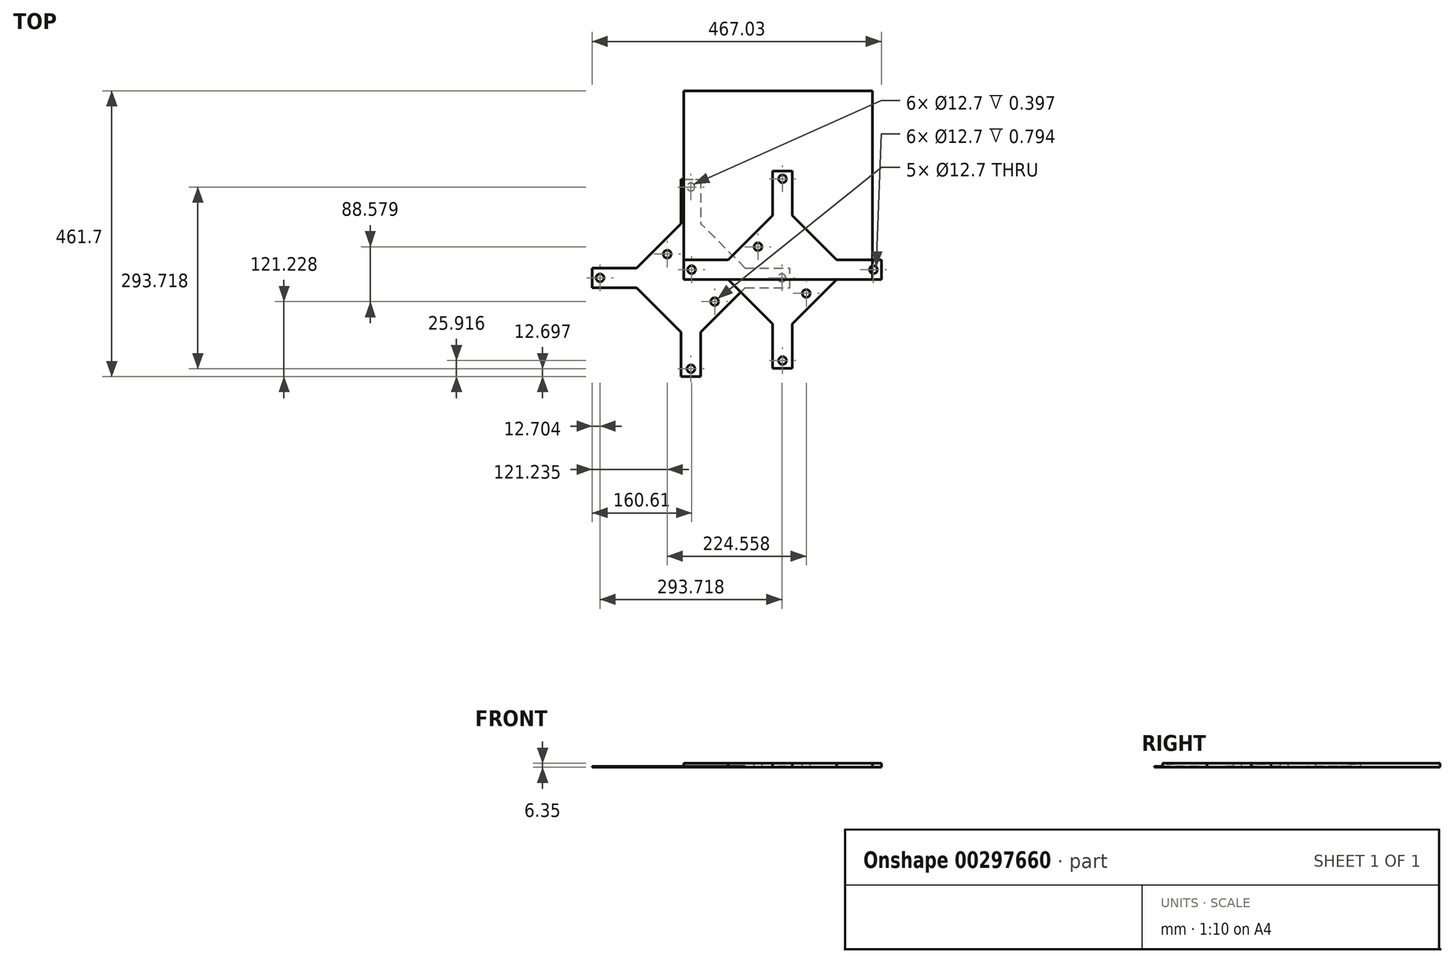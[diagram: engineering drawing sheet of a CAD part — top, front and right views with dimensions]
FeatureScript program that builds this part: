
annotation { "Feature Type Name" : "Feature", "Feature Type Description" : "" }
export const myFeature = defineFeature(function(context is Context, id is Id, definition is map)
    precondition{}
    {
        {
            var Q0;
            Q0=qCreatedBy(makeId("Top.planeOp"),FACE);
            var sketch = newSketch(context, id + "F0", { "sketchPlane" : qUnion([Q0])});
            skLineSegment(sketch, "E0.bottom", {"start": v(0, 0) * mm, "end": v(304.8, 0) * mm});
            skLineSegment(sketch, "E0.top", {"start": v(0, 304.8) * mm, "end": v(304.8, 304.8) * mm});
            skLineSegment(sketch, "E0.left", {"start": v(0, 0) * mm, "end": v(0, 304.8) * mm});
            skLineSegment(sketch, "E0.right", {"start": v(304.8, 0) * mm, "end": v(304.8, 304.8) * mm});
            skSolve(sketch);
        }
        {
            var Q0;
            Q0 = qSketchRegion(id + "F0", true);
            extrude(context, id + "F1", {"entities" : qUnion([Q0]), "depth" : 6.35 * mm});
        }
        {
            var Q0;
            Q0=qCreatedBy(makeId("Top.planeOp"),FACE);
            var sketch = newSketch(context, id + "F2", { "sketchPlane" : qUnion([Q0])});
            skLineSegment(sketch, "E1.bottom", {"start": v(0, 0) * mm, "end": v(71.84, 0) * mm});
            skLineSegment(sketch, "E1.top", {"start": v(0, 31.75) * mm, "end": v(71.84, 31.75) * mm});
            skLineSegment(sketch, "E1.left", {"start": v(0, 0) * mm, "end": v(0, 31.75) * mm});
            skLineSegment(sketch, "E2", {"start": v(0, 0) * mm, "end": v(143.68, -143.68) * mm, "construction": true});
            skLineSegment(sketch, "E3.bottom", {"start": v(143.68, 0) * mm, "end": v(143.68, 0) * mm});
            skLineSegment(sketch, "E3.top", {"start": v(143.68, -143.68) * mm, "end": v(143.68, -143.68) * mm});
            skLineSegment(sketch, "E4", {"start": v(143.68, -143.68) * mm, "end": v(175.43, -143.68) * mm});
            skLineSegment(sketch, "E5", {"start": v(175.43, -143.68) * mm, "end": v(175.43, -71.84) * mm});
            skLineSegment(sketch, "E6.right", {"start": v(175.43, 0) * mm, "end": v(175.43, 0) * mm});
            skLineSegment(sketch, "E7", {"start": v(0, 31.75) * mm, "end": v(143.68, 175.43) * mm, "construction": true});
            skLineSegment(sketch, "E8", {"start": v(143.68, 175.43) * mm, "end": v(143.68, 103.6) * mm});
            skLineSegment(sketch, "E9", {"start": v(0, 31.75) * mm, "end": v(-15.87, 15.88) * mm, "construction": true});
            skPoint(sketch, "E9.endSnap0", {"position": v(143.68, 15.88) * mm});
            skLineSegment(sketch, "E10", {"start": v(-15.87, 15.88) * mm, "end": v(0, 0) * mm, "construction": true});
            skLineSegment(sketch, "E11", {"start": v(143.68, 31.75) * mm, "end": v(143.68, 0) * mm, "construction": true});
            skLineSegment(sketch, "E12", {"start": v(175.43, 0) * mm, "end": v(143.68, 0) * mm, "construction": true});
            skLineSegment(sketch, "E13", {"start": v(143.68, 31.75) * mm, "end": v(175.43, 31.75) * mm, "construction": true});
            skLineSegment(sketch, "E14", {"start": v(143.68, -71.84) * mm, "end": v(143.68, -143.68) * mm});
            skLineSegment(sketch, "E15", {"start": v(143.68, 175.43) * mm, "end": v(175.43, 175.43) * mm});
            skLineSegment(sketch, "E16", {"start": v(175.43, 175.43) * mm, "end": v(175.43, 103.6) * mm});
            skLineSegment(sketch, "E17", {"start": v(175.43, 175.43) * mm, "end": v(319.12, 31.75) * mm, "construction": true});
            skLineSegment(sketch, "E18.bottom", {"start": v(247.28, 0) * mm, "end": v(319.12, 0) * mm});
            skLineSegment(sketch, "E18.top", {"start": v(247.28, 31.75) * mm, "end": v(319.12, 31.75) * mm});
            skLineSegment(sketch, "E18.right", {"start": v(319.12, 0) * mm, "end": v(319.12, 31.75) * mm});
            skLineSegment(sketch, "E19", {"start": v(175.43, 31.75) * mm, "end": v(175.43, 0) * mm, "construction": true});
            skLineSegment(sketch, "E20", {"start": v(71.84, 0) * mm, "end": v(143.68, -71.84) * mm});
            skLineSegment(sketch, "E21", {"start": v(175.43, -71.84) * mm, "end": v(247.28, 0) * mm});
            skLineSegment(sketch, "E22", {"start": v(247.28, 31.75) * mm, "end": v(175.43, 103.6) * mm});
            skLineSegment(sketch, "E23", {"start": v(143.68, 103.6) * mm, "end": v(71.84, 31.75) * mm});
            skPoint(sketch, "E24.orphan", {"position": v(175.43, 31.75) * mm});
            skLineSegment(sketch, "E25", {"start": v(71.84, 31.75) * mm, "end": v(143.68, 31.75) * mm, "construction": true});
            skLineSegment(sketch, "E26", {"start": v(143.68, 103.6) * mm, "end": v(143.68, 31.75) * mm, "construction": true});
            skLineSegment(sketch, "E27", {"start": v(175.43, 103.6) * mm, "end": v(175.43, 31.75) * mm, "construction": true});
            skLineSegment(sketch, "E28", {"start": v(247.28, 31.75) * mm, "end": v(175.43, 31.75) * mm, "construction": true});
            skLineSegment(sketch, "E29", {"start": v(247.28, 0) * mm, "end": v(175.43, 0) * mm, "construction": true});
            skLineSegment(sketch, "E30", {"start": v(143.68, 0) * mm, "end": v(143.68, -71.84) * mm, "construction": true});
            skLineSegment(sketch, "E31", {"start": v(175.43, 0) * mm, "end": v(175.43, -71.84) * mm, "construction": true});
            skLineSegment(sketch, "E32", {"start": v(143.68, 0) * mm, "end": v(71.84, 0) * mm, "construction": true});
            skSolve(sketch);
        }
        {
            var Q0;
            Q0 = qSketchRegion(id + "F2", true);
            extrude(context, id + "F3", {"entities" : qUnion([Q0]), "depth" : 6.35 * mm});
        }
        {
            var Q0;
            Q0=makeQuery(id+"F3.opExtrude","CAP_FACE",FACE,{"disambiguationData":[OSD([sQuery(id+"F2.wireOp",EDGE,"E1.bottom"),sQuery(id+"F2.wireOp",EDGE,"E1.top"),sQuery(id+"F2.wireOp",EDGE,"E1.left"),sQuery(id+"F2.wireOp",EDGE,"E4"),sQuery(id+"F2.wireOp",EDGE,"E5"),sQuery(id+"F2.wireOp",EDGE,"E8"),sQuery(id+"F2.wireOp",EDGE,"E14"),sQuery(id+"F2.wireOp",EDGE,"E15"),sQuery(id+"F2.wireOp",EDGE,"E16"),sQuery(id+"F2.wireOp",EDGE,"E18.bottom"),sQuery(id+"F2.wireOp",EDGE,"E18.top"),sQuery(id+"F2.wireOp",EDGE,"E18.right"),sQuery(id+"F2.wireOp",EDGE,"E20"),sQuery(id+"F2.wireOp",EDGE,"E21"),sQuery(id+"F2.wireOp",EDGE,"E22"),sQuery(id+"F2.wireOp",EDGE,"E23")])],"isStart":false});
            var sketch = newSketch(context, id + "F4", { "sketchPlane" : qUnion([Q0])});
            skCircle(sketch, "E33", {"center": v(197.88, -22.45) * mm, "radius": 6.35 * mm});
            skCircle(sketch, "E34", {"center": v(119.94, 52.9) * mm, "radius": 6.35 * mm});
            skLineSegment(sketch, "E35", {"start": v(211.36, 67.67) * mm, "end": v(107.76, -35.92) * mm, "construction": true});
            skSolve(sketch);
        }
        {
            var Q0;
            Q0 = qSketchRegion(id + "F4", true);
            extrude(context, id + "F5", {"entities" : qUnion([Q0]), "operationType" : NewBodyOperationType.REMOVE, "oppositeDirection" : true, "depth" : 25.4 * mm});
        }
        {
            var Q0;
            Q0=makeQuery(id+"F3.opExtrude","CAP_FACE",FACE,{"disambiguationData":[OSD([sQuery(id+"F2.wireOp",EDGE,"E1.bottom"),sQuery(id+"F2.wireOp",EDGE,"E1.top"),sQuery(id+"F2.wireOp",EDGE,"E1.left"),sQuery(id+"F2.wireOp",EDGE,"E4"),sQuery(id+"F2.wireOp",EDGE,"E5"),sQuery(id+"F2.wireOp",EDGE,"E8"),sQuery(id+"F2.wireOp",EDGE,"E14"),sQuery(id+"F2.wireOp",EDGE,"E15"),sQuery(id+"F2.wireOp",EDGE,"E16"),sQuery(id+"F2.wireOp",EDGE,"E18.bottom"),sQuery(id+"F2.wireOp",EDGE,"E18.top"),sQuery(id+"F2.wireOp",EDGE,"E18.right"),sQuery(id+"F2.wireOp",EDGE,"E20"),sQuery(id+"F2.wireOp",EDGE,"E21"),sQuery(id+"F2.wireOp",EDGE,"E22"),sQuery(id+"F2.wireOp",EDGE,"E23")])],"isStart":false});
            var sketch = newSketch(context, id + "F6", { "sketchPlane" : qUnion([Q0])});
            skCircle(sketch, "E36", {"center": v(12.7, 15.88) * mm, "radius": 6.35 * mm});
            skCircle(sketch, "E37", {"center": v(159.56, 162.73) * mm, "radius": 6.35 * mm});
            skCircle(sketch, "E38", {"center": v(306.42, 15.88) * mm, "radius": 6.35 * mm});
            skCircle(sketch, "E39", {"center": v(159.56, -130.98) * mm, "radius": 6.35 * mm});
            skSolve(sketch);
        }
        {
            var Q0;
            Q0 = qSketchRegion(id + "F6", true);
            extrude(context, id + "F7", {"entities" : qUnion([Q0]), "operationType" : NewBodyOperationType.REMOVE, "oppositeDirection" : true, "depth" : 0.8 * mm});
        }
        {
            var Q0;
            Q0=qCreatedBy(makeId("Top.planeOp"),FACE);
            var sketch = newSketch(context, id + "F8", { "sketchPlane" : qUnion([Q0])});
            skLineSegment(sketch, "E40.bottom", {"start": v(-147.9, -13.22) * mm, "end": v(-76.06, -13.22) * mm});
            skLineSegment(sketch, "E40.top", {"start": v(-147.9, 18.53) * mm, "end": v(-76.06, 18.53) * mm});
            skLineSegment(sketch, "E40.left", {"start": v(-147.9, -13.22) * mm, "end": v(-147.9, 18.53) * mm});
            skLineSegment(sketch, "E41", {"start": v(-147.9, -13.22) * mm, "end": v(-4.22, -156.9) * mm, "construction": true});
            skLineSegment(sketch, "E42.bottom", {"start": v(-4.22, -13.22) * mm, "end": v(-4.22, -13.22) * mm});
            skLineSegment(sketch, "E42.top", {"start": v(-4.22, -156.9) * mm, "end": v(-4.22, -156.9) * mm});
            skLineSegment(sketch, "E43", {"start": v(-4.22, -156.9) * mm, "end": v(27.53, -156.9) * mm});
            skLineSegment(sketch, "E44", {"start": v(27.53, -156.9) * mm, "end": v(27.53, -85.06) * mm});
            skLineSegment(sketch, "E45.right", {"start": v(27.53, -13.22) * mm, "end": v(27.53, -13.22) * mm});
            skLineSegment(sketch, "E46", {"start": v(-147.9, 18.53) * mm, "end": v(-4.22, 162.22) * mm, "construction": true});
            skLineSegment(sketch, "E47", {"start": v(-4.22, 162.22) * mm, "end": v(-4.22, 90.37) * mm});
            skLineSegment(sketch, "E48", {"start": v(-147.9, 18.53) * mm, "end": v(-163.78, 2.66) * mm, "construction": true});
            skPoint(sketch, "E48.endSnap0", {"position": v(-4.22, 2.66) * mm});
            skLineSegment(sketch, "E49", {"start": v(-163.78, 2.66) * mm, "end": v(-147.9, -13.22) * mm, "construction": true});
            skLineSegment(sketch, "E50", {"start": v(-4.22, 18.53) * mm, "end": v(-4.22, -13.22) * mm, "construction": true});
            skLineSegment(sketch, "E51", {"start": v(27.53, -13.22) * mm, "end": v(-4.22, -13.22) * mm, "construction": true});
            skLineSegment(sketch, "E52", {"start": v(-4.22, 18.53) * mm, "end": v(27.53, 18.53) * mm, "construction": true});
            skLineSegment(sketch, "E53", {"start": v(-4.22, -85.06) * mm, "end": v(-4.22, -156.9) * mm});
            skLineSegment(sketch, "E54", {"start": v(-4.22, 162.22) * mm, "end": v(27.53, 162.22) * mm});
            skLineSegment(sketch, "E55", {"start": v(27.53, 162.22) * mm, "end": v(27.53, 90.37) * mm});
            skLineSegment(sketch, "E56", {"start": v(27.53, 162.22) * mm, "end": v(171.21, 18.53) * mm, "construction": true});
            skLineSegment(sketch, "E57.bottom", {"start": v(99.37, -13.22) * mm, "end": v(171.21, -13.22) * mm});
            skLineSegment(sketch, "E57.top", {"start": v(99.37, 18.53) * mm, "end": v(171.21, 18.53) * mm});
            skLineSegment(sketch, "E57.right", {"start": v(171.21, -13.22) * mm, "end": v(171.21, 18.53) * mm});
            skLineSegment(sketch, "E58", {"start": v(27.53, 18.53) * mm, "end": v(27.53, -13.22) * mm, "construction": true});
            skLineSegment(sketch, "E59", {"start": v(-76.06, -13.22) * mm, "end": v(-4.22, -85.06) * mm});
            skLineSegment(sketch, "E60", {"start": v(27.53, -85.06) * mm, "end": v(99.37, -13.22) * mm});
            skLineSegment(sketch, "E61", {"start": v(99.37, 18.53) * mm, "end": v(27.53, 90.37) * mm});
            skLineSegment(sketch, "E62", {"start": v(-4.22, 90.37) * mm, "end": v(-76.06, 18.53) * mm});
            skPoint(sketch, "E63.orphan", {"position": v(27.53, 18.53) * mm});
            skLineSegment(sketch, "E64", {"start": v(-76.06, 18.53) * mm, "end": v(-4.22, 18.53) * mm, "construction": true});
            skLineSegment(sketch, "E65", {"start": v(-4.22, 90.37) * mm, "end": v(-4.22, 18.53) * mm, "construction": true});
            skLineSegment(sketch, "E66", {"start": v(27.53, 90.37) * mm, "end": v(27.53, 18.53) * mm, "construction": true});
            skLineSegment(sketch, "E67", {"start": v(99.37, 18.53) * mm, "end": v(27.53, 18.53) * mm, "construction": true});
            skLineSegment(sketch, "E68", {"start": v(99.37, -13.22) * mm, "end": v(27.53, -13.22) * mm, "construction": true});
            skLineSegment(sketch, "E69", {"start": v(-4.22, -13.22) * mm, "end": v(-4.22, -85.06) * mm, "construction": true});
            skLineSegment(sketch, "E70", {"start": v(27.53, -13.22) * mm, "end": v(27.53, -85.06) * mm, "construction": true});
            skLineSegment(sketch, "E71", {"start": v(-4.22, -13.22) * mm, "end": v(-76.06, -13.22) * mm, "construction": true});
            skSolve(sketch);
        }
        {
            var Q0;
            Q0=makeQuery(id+"F8.imprint","IMPRINT",FACE,{"disambiguationData":[TD([[makeQuery(id+"F8.imprint","IMPRINT",EDGE,{"derivedFrom":sQuery(id+"F8.wireOp",EDGE,"E40.bottom")}),1.0]])]});
            extrude(context, id + "F9", {"entities" : qUnion([Q0]), "depth" : 1.59 * mm});
        }
        {
            var Q0;
            Q0=makeQuery(id+"F9.opExtrude","CAP_FACE",FACE,{"disambiguationData":[OSD([sQuery(id+"F8.wireOp",EDGE,"E40.bottom"),sQuery(id+"F8.wireOp",EDGE,"E40.top"),sQuery(id+"F8.wireOp",EDGE,"E40.left"),sQuery(id+"F8.wireOp",EDGE,"E43"),sQuery(id+"F8.wireOp",EDGE,"E44"),sQuery(id+"F8.wireOp",EDGE,"E47"),sQuery(id+"F8.wireOp",EDGE,"E53"),sQuery(id+"F8.wireOp",EDGE,"E54"),sQuery(id+"F8.wireOp",EDGE,"E55"),sQuery(id+"F8.wireOp",EDGE,"E57.bottom"),sQuery(id+"F8.wireOp",EDGE,"E57.top"),sQuery(id+"F8.wireOp",EDGE,"E57.right"),sQuery(id+"F8.wireOp",EDGE,"E59"),sQuery(id+"F8.wireOp",EDGE,"E60"),sQuery(id+"F8.wireOp",EDGE,"E61"),sQuery(id+"F8.wireOp",EDGE,"E62")])],"isStart":false});
            var sketch = newSketch(context, id + "F10", { "sketchPlane" : qUnion([Q0])});
            skLineSegment(sketch, "E72", {"start": v(-40.14, -49.14) * mm, "end": v(63.45, 54.45) * mm, "construction": true});
            skCircle(sketch, "E73", {"center": v(49.98, -35.67) * mm, "radius": 6.35 * mm});
            skLineSegment(sketch, "E74", {"start": v(99.37, -13.22) * mm, "end": v(47.57, 38.58) * mm, "construction": true});
            skCircle(sketch, "E75.MirrorC", {"center": v(-26.67, 40.98) * mm, "radius": 6.35 * mm});
            skSolve(sketch);
        }
        {
            var Q0;
            Q0 = qSketchRegion(id + "F10", true);
            extrude(context, id + "F11", {"entities" : qUnion([Q0]), "operationType" : NewBodyOperationType.REMOVE, "oppositeDirection" : true, "depth" : 25.4 * mm});
        }
        {
            var Q0;
            Q0=makeQuery(id+"F9.opExtrude","CAP_FACE",FACE,{"disambiguationData":[OSD([sQuery(id+"F8.wireOp",EDGE,"E40.bottom"),sQuery(id+"F8.wireOp",EDGE,"E40.top"),sQuery(id+"F8.wireOp",EDGE,"E40.left"),sQuery(id+"F8.wireOp",EDGE,"E43"),sQuery(id+"F8.wireOp",EDGE,"E44"),sQuery(id+"F8.wireOp",EDGE,"E47"),sQuery(id+"F8.wireOp",EDGE,"E53"),sQuery(id+"F8.wireOp",EDGE,"E54"),sQuery(id+"F8.wireOp",EDGE,"E55"),sQuery(id+"F8.wireOp",EDGE,"E57.bottom"),sQuery(id+"F8.wireOp",EDGE,"E57.top"),sQuery(id+"F8.wireOp",EDGE,"E57.right"),sQuery(id+"F8.wireOp",EDGE,"E59"),sQuery(id+"F8.wireOp",EDGE,"E60"),sQuery(id+"F8.wireOp",EDGE,"E61"),sQuery(id+"F8.wireOp",EDGE,"E62")])],"isStart":false});
            var sketch = newSketch(context, id + "F12", { "sketchPlane" : qUnion([Q0])});
            skCircle(sketch, "E76", {"center": v(11.65, 149.52) * mm, "radius": 6.35 * mm});
            skCircle(sketch, "E77", {"center": v(-135.2, 2.66) * mm, "radius": 6.35 * mm});
            skLineSegment(sketch, "E78", {"start": v(63.45, 54.45) * mm, "end": v(-40.14, -49.14) * mm, "construction": true});
            skCircle(sketch, "E79.MirrorC", {"center": v(158.51, 2.66) * mm, "radius": 6.35 * mm});
            skCircle(sketch, "E80.MirrorC", {"center": v(11.65, -144.2) * mm, "radius": 6.35 * mm});
            skSolve(sketch);
        }
        {
            var Q0;
            Q0 = qSketchRegion(id + "F12", true);
            extrude(context, id + "F13", {"entities" : qUnion([Q0]), "operationType" : NewBodyOperationType.REMOVE, "oppositeDirection" : true, "depth" : 0.4 * mm});
        }
        {
            var Q0;
            Q0=qCreatedBy(makeId("Top.planeOp"),FACE);
            var sketch = newSketch(context, id + "F14", { "sketchPlane" : qUnion([Q0])});
            skLineSegment(sketch, "E81.bottom", {"start": v(0, 0) * mm, "end": v(304.8, 0) * mm});
            skLineSegment(sketch, "E81.top", {"start": v(0, 304.8) * mm, "end": v(304.8, 304.8) * mm});
            skLineSegment(sketch, "E81.left", {"start": v(0, 0) * mm, "end": v(0, 304.8) * mm});
            skLineSegment(sketch, "E81.right", {"start": v(304.8, 0) * mm, "end": v(304.8, 304.8) * mm});
            skSolve(sketch);
        }
        {
            var Q0;
            Q0 = qSketchRegion(id + "F14", true);
            extrude(context, id + "F15", {"entities" : qUnion([Q0]), "depth" : 6.35 * mm});
        }
    });
